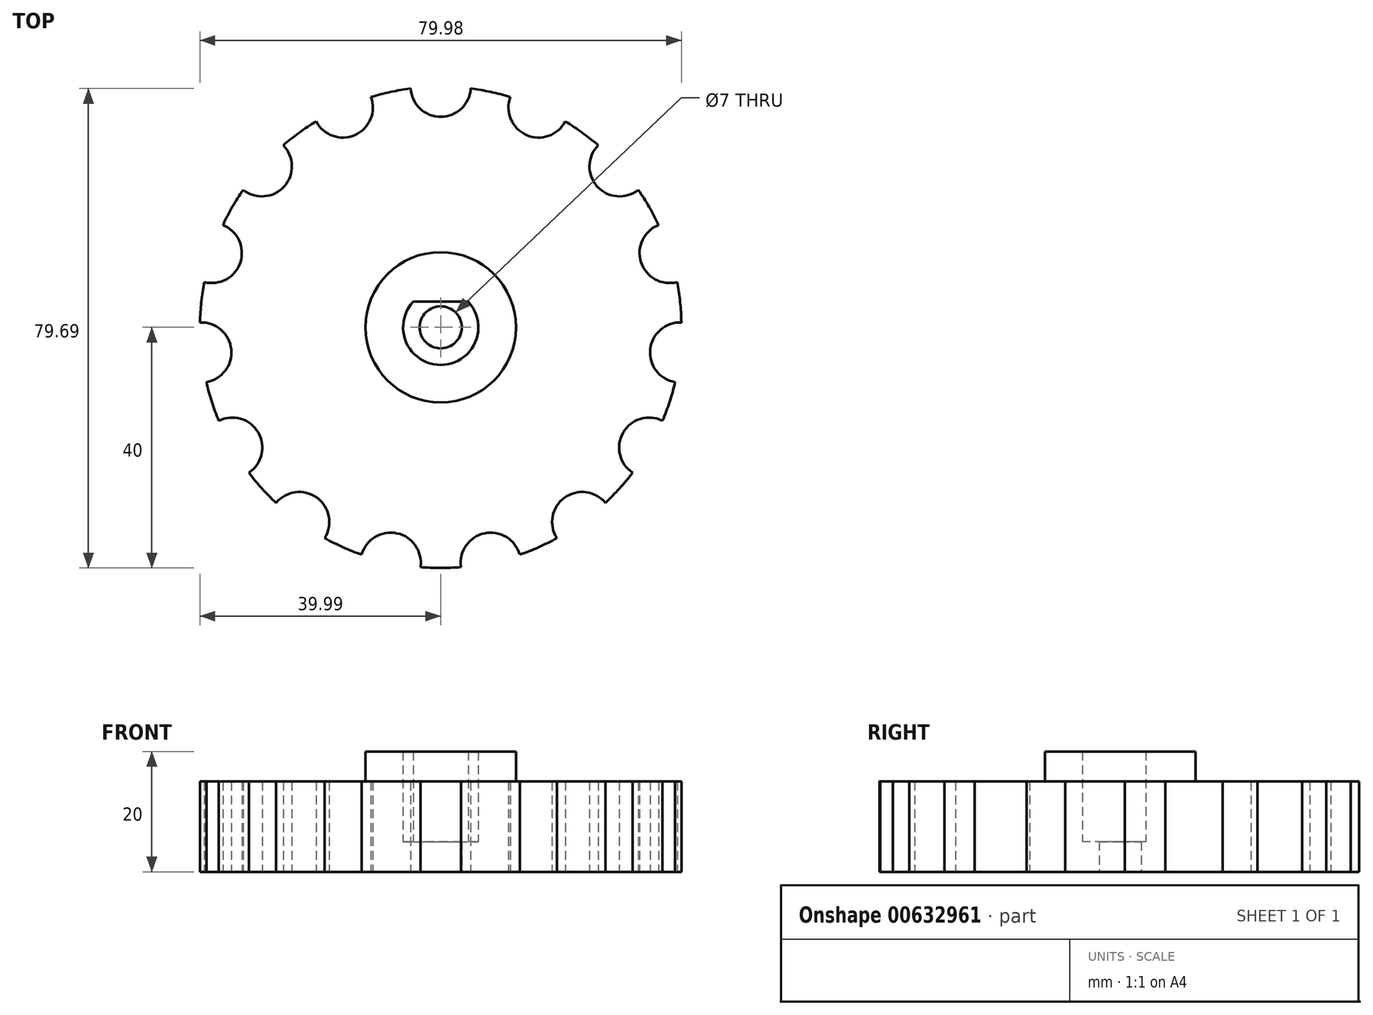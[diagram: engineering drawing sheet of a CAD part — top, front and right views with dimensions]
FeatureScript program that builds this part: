
annotation { "Feature Type Name" : "Feature", "Feature Type Description" : "" }
export const myFeature = defineFeature(function(context is Context, id is Id, definition is map)
    precondition{}
    {
        {
            var Q0;
            Q0=qCreatedBy(makeId("Top.planeOp"),FACE);
            var sketch = newSketch(context, id + "F0", { "sketchPlane" : qUnion([Q0])});
            skCircle(sketch, "E0", {"center": v(0, 0) * mm, "radius": 40 * mm});
            skArc(sketch, "E1", {"start": v(-4.58, 4.25) * mm, "mid": v(0, -6.25) * mm, "end": v(4.58, 4.25) * mm});
            skLineSegment(sketch, "E2", {"start": v(-4.58, 4.25) * mm, "end": v(4.58, 4.25) * mm});
            skCircle(sketch, "E3", {"center": v(0, 40) * mm, "radius": 5 * mm});
            skCircle(sketch, "E4.1.0", {"center": v(-16.27, 36.54) * mm, "radius": 5 * mm});
            skCircle(sketch, "E4.2.0", {"center": v(-29.73, 26.77) * mm, "radius": 5 * mm});
            skCircle(sketch, "E4.3.0", {"center": v(-38.04, 12.36) * mm, "radius": 5 * mm});
            skCircle(sketch, "E4.4.0", {"center": v(-39.78, -4.18) * mm, "radius": 5 * mm});
            skCircle(sketch, "E4.5.0", {"center": v(-34.64, -20) * mm, "radius": 5 * mm});
            skCircle(sketch, "E4.6.0", {"center": v(-23.51, -32.36) * mm, "radius": 5 * mm});
            skCircle(sketch, "E4.7.0", {"center": v(-8.32, -39.13) * mm, "radius": 5 * mm});
            skCircle(sketch, "E4.8.0", {"center": v(8.32, -39.13) * mm, "radius": 5 * mm});
            skCircle(sketch, "E5", {"center": v(0, 0) * mm, "radius": 12.5 * mm});
            skCircle(sketch, "E6.1.9.0", {"center": v(23.51, -32.36) * mm, "radius": 5 * mm});
            skCircle(sketch, "E6.1.10.0", {"center": v(34.64, -20) * mm, "radius": 5 * mm});
            skCircle(sketch, "E6.1.11.0", {"center": v(39.78, -4.18) * mm, "radius": 5 * mm});
            skCircle(sketch, "E6.1.12.0", {"center": v(38.04, 12.36) * mm, "radius": 5 * mm});
            skCircle(sketch, "E6.1.13.0", {"center": v(29.73, 26.77) * mm, "radius": 5 * mm});
            skCircle(sketch, "E6.1.14.0", {"center": v(16.27, 36.54) * mm, "radius": 5 * mm});
            skSolve(sketch);
        }
        {
            var Q0;
            Q0=makeQuery(id+"F0.imprint","IMPRINT",FACE,{"disambiguationData":[TD([[makeQuery(id+"F0.imprint","IMPRINT",EDGE,{"derivedFrom":sQuery(id+"F0.wireOp",EDGE,"E5")}),-1.0]])]});
            extrude(context, id + "F1", {"entities" : qUnion([Q0]), "depth" : 15 * mm, "offsetDistance" : 25 * mm});
        }
        {
            var Q0;
            Q0=makeQuery(id+"F0.imprint","IMPRINT",FACE,{"disambiguationData":[TD([[makeQuery(id+"F0.imprint","IMPRINT",EDGE,{"derivedFrom":sQuery(id+"F0.wireOp",EDGE,"E1")}),-1.0]])]});
            extrude(context, id + "F2", {"entities" : qUnion([Q0]), "operationType" : NewBodyOperationType.ADD, "depth" : 20 * mm, "offsetDistance" : 25 * mm});
        }
        {
            var Q0;
            Q0=qCreatedBy(makeId("Top.planeOp"),FACE);
            var sketch = newSketch(context, id + "F3", { "sketchPlane" : qUnion([Q0])});
            skCircle(sketch, "E7", {"center": v(0, 0) * mm, "radius": 10 * mm});
            skCircle(sketch, "E8", {"center": v(0, 0) * mm, "radius": 3.5 * mm});
            skSolve(sketch);
        }
        {
            var Q0;
            Q0 = qSketchRegion(id + "F3", true);
            extrude(context, id + "F4", {"entities" : qUnion([Q0]), "operationType" : NewBodyOperationType.ADD, "depth" : 5 * mm, "offsetDistance" : 25 * mm});
        }
        {
            var Q0;
            Q0=makeQuery(id+"F0.imprint","IMPRINT",FACE,{"disambiguationData":[TD([[makeQuery(id+"F0.imprint","IMPRINT",EDGE,{"derivedFrom":sQuery(id+"F0.wireOp",EDGE,"E5")}),-1.0]])]});
            extrude(context, id + "F5", {"entities" : qUnion([Q0]), "depth" : 15 * mm, "offsetDistance" : 25 * mm});
        }
        {
            var Q0;
            Q0=makeQuery(id+"F0.imprint","IMPRINT",FACE,{"disambiguationData":[TD([[makeQuery(id+"F0.imprint","IMPRINT",EDGE,{"derivedFrom":sQuery(id+"F0.wireOp",EDGE,"E1")}),-1.0]])]});
            extrude(context, id + "F6", {"entities" : qUnion([Q0]), "operationType" : NewBodyOperationType.ADD, "depth" : 20 * mm, "offsetDistance" : 25 * mm});
        }
    });
